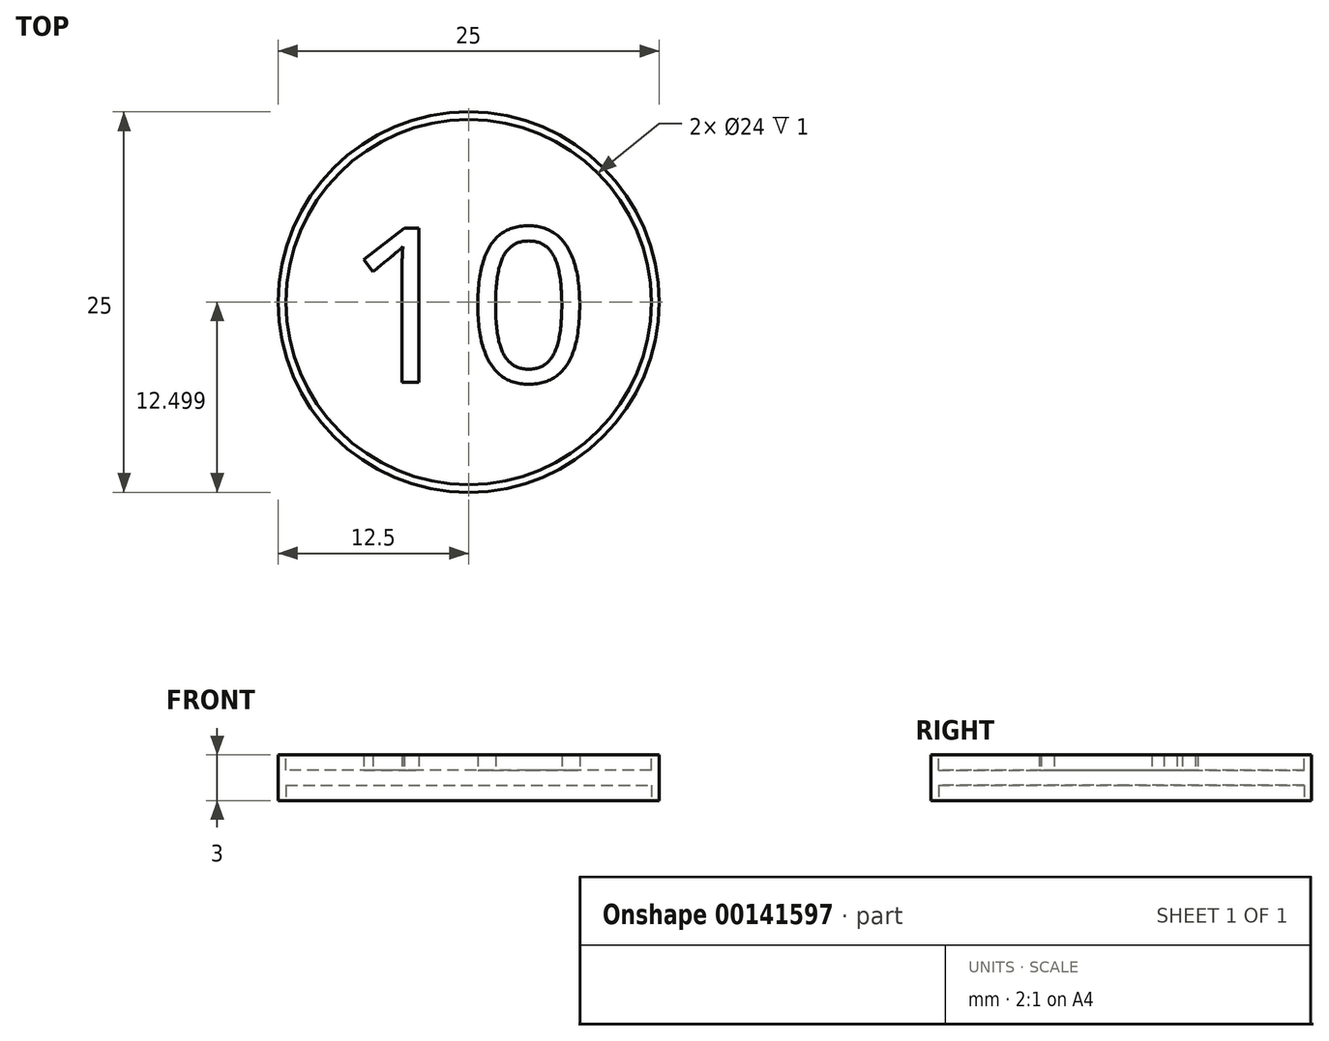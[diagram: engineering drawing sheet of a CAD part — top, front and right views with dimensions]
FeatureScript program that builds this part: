
annotation { "Feature Type Name" : "Feature", "Feature Type Description" : "" }
export const myFeature = defineFeature(function(context is Context, id is Id, definition is map)
    precondition{}
    {
        {
            assignVariable(context, id + "F0", {"name" : "Thickness", "anyValue" : 3});
        }
        {
            assignVariable(context, id + "F1", {"name" : "ImpressionDepth", "anyValue" : 1});
        }
        {
            var Q0;
            Q0=qCreatedBy(makeId("Top.planeOp"),FACE);
            var sketch = newSketch(context, id + "F2", { "sketchPlane" : qUnion([Q0])});
            skCircle(sketch, "E0", {"center": v(0, 0.16) * mm, "radius": 12.5 * mm});
            skSolve(sketch);
        }
        {
            var Q0;
            Q0 = qSketchRegion(id + "F2", true);
            var Q1;
            Q1 = qConstructionFilter(qBodyType(qCreatedBy(id + "F2" ,EDGE), BodyType.WIRE), ConstructionObject.NO);
            extrude(context, id + "F3", {"entities" : qUnion([Q0]), "surfaceEntities" : qUnion([Q1]), "depth" : (getVariable(context, 'Thickness')) * mm});
        }
        {
            var Q0;
            Q0=makeQuery(id+"F3.opExtrude","CAP_FACE",FACE,{"disambiguationData":[OSD([sQuery(id+"F2.wireOp",EDGE,"E0")])],"isStart":false});
            var sketch = newSketch(context, id + "F4", { "sketchPlane" : qUnion([Q0])});
            skCircle(sketch, "E1.0", {"center": v(0, 0.16) * mm, "radius": 12 * mm});
            skSolve(sketch);
        }
        {
            var Q0;
            Q0 = qSketchRegion(id + "F4", true);
            extrude(context, id + "F5", {"entities" : qUnion([Q0]), "operationType" : NewBodyOperationType.REMOVE, "oppositeDirection" : true, "depth" : (getVariable(context, 'ImpressionDepth')) * mm});
        }
        {
            var Q0;
            Q0=makeQuery(id+"F3.opExtrude","CAP_FACE",FACE,{"disambiguationData":[OSD([sQuery(id+"F2.wireOp",EDGE,"E0")])],"isStart":true});
            var sketch = newSketch(context, id + "F6", { "sketchPlane" : qUnion([Q0])});
            skCircle(sketch, "E2.0", {"center": v(0, -0.16) * mm, "radius": 12 * mm});
            skSolve(sketch);
        }
        {
            var Q0;
            Q0 = qSketchRegion(id + "F6", true);
            extrude(context, id + "F7", {"entities" : qUnion([Q0]), "operationType" : NewBodyOperationType.REMOVE, "oppositeDirection" : true, "depth" : (getVariable(context, 'ImpressionDepth')) * mm});
        }
        {
            var Q0;
            Q0=makeQuery(id+"F5.boolean.opBoolean","COPY",FACE,{"derivedFrom":makeQuery(id+"F5.opExtrude","CAP_FACE",FACE,{"disambiguationData":[OSD([sQuery(id+"F4.wireOp",EDGE,"E1.0")])],"isStart":false})});
            var sketch = newSketch(context, id + "F8", { "sketchPlane" : qUnion([Q0])});
            skText(sketch, "E3", { "text": "10", "fontName": "OpenSans-Regular.ttf"});
            skPoint(sketch, "E4", {"position": v(0, 0) * mm});
            const initialGuessF8  = {"E3": [-0.0082, -0.0051, 1, 0, 0.0102]};
            skSetInitialGuess(sketch, initialGuessF8);
            skSolve(sketch);
        }
        {
            var Q0;
            Q0 = qSketchRegion(id + "F8", true);
            extrude(context, id + "F9", {"entities" : qUnion([Q0]), "operationType" : NewBodyOperationType.ADD, "depth" : (getVariable(context, 'ImpressionDepth')) * mm});
        }
    });
